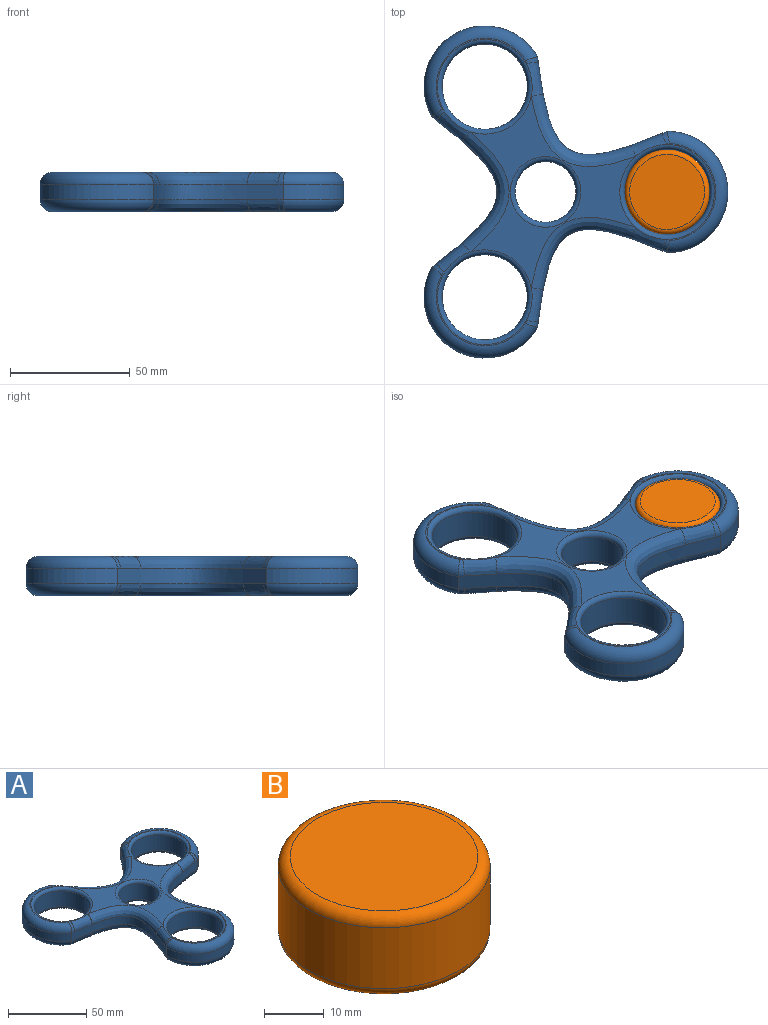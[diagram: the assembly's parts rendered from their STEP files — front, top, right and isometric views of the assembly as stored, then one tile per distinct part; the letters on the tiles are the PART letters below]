
ASSEMBLY  parts=2 mates=1
PART A: 62 faces, bbox 143x131.2x18.5 mm
  f0: plane 79.89x69.2mm, normal (0,0,1), area 1351.3mm2, adj f22,f23,f24,f25,f46,f53,f58
  f1: plane 37.59x30.43mm, normal (0,0,1), area 31.6mm2, adj f24,f57,f59,f61
  f2: plane 37.59x30.43mm, normal (0,0,1), area 31.6mm2, adj f25,f45,f47,f49
  f3: plane 79.89x69.19mm, normal (0,0,-1), area 1351.3mm2, adj f18,f19,f20,f21,f28,f35,f40
  f4: plane 37.59x30.43mm, normal (0,0,-1), area 31.6mm2, adj f21,f27,f29,f31
  f5: plane 37.59x30.43mm, normal (0,0,-1), area 31.6mm2, adj f20,f39,f41,f43
  f6: extruded ~54.2x40.99mm, area 540.5mm2, adj f7,f14,f26,f27,f28,f30,f32,f44
  f7: cylinder r=25.4mm len=50.8mm, axis (0,0,-1), area 506.7mm2, adj f6,f8,f34,f52
  f8: extruded ~54.2x40.99mm, area 540.5mm2, adj f7,f9,f36,f38,f40,f42,f43,f54
  f9: cylinder r=25.4mm len=47.4mm, axis (0,0,-1), area 506.7mm2, adj f8,f10,f41,f59
  f10: extruded ~62.59x27.08mm, area 540.5mm2, adj f9,f14,f31,f33,f35,f37,f39,f49
  f11: cylinder r=17.78mm len=35.56mm, axis (0,0,-1), area 1390.4mm2, adj f20,f24
  f12: cylinder r=17.78mm len=35.56mm, axis (0,0,-1), area 1390.4mm2, adj f21,f25
  f13: cylinder r=12.7mm len=25.4mm, axis (0,0,-1), area 993.1mm2, adj f18,f22
  f14: cylinder r=25.4mm len=47.4mm, axis (0,0,-1), area 506.7mm2, adj f6,f10,f29,f47
  f15: cylinder r=17.78mm len=35.56mm, axis (0,0,-1), area 1390.4mm2, adj f19,f23
  f16: plane 40.6x20.55mm, normal (0,0,1), area 31.6mm2, adj f23,f50,f52,f54
  f17: plane 40.6x20.55mm, normal (0,0,-1), area 31.6mm2, adj f19,f32,f34,f36
  f18: torus R=14.73mm, axis (0,0,1), area 269.5mm2, adj f3,f13
  f19: torus R=19.81mm, axis (0,0,1), area 371.4mm2, adj f3,f15,f17,f30,f38
  f20: torus R=19.81mm, axis (0,0,1), area 371.4mm2, adj f3,f5,f11,f37,f42
  f21: torus R=19.81mm, axis (0,0,1), area 371.4mm2, adj f3,f4,f12,f26,f33
  f22: torus R=14.73mm, axis (0,0,1), area 269.5mm2, adj f0,f13
  f23: torus R=19.81mm, axis (0,0,1), area 371.4mm2, adj f0,f15,f16,f48,f56
  f24: torus R=19.81mm, axis (0,0,1), area 371.4mm2, adj f0,f1,f11,f55,f60
  f25: torus R=19.81mm, axis (0,0,1), area 371.4mm2, adj f0,f2,f12,f44,f51
  f26: bspline ~17.43x8.27mm, area 97.1mm2, adj f6,f21,f27,f28
  f27: bspline ~8.75x6.12mm, area 14.4mm2, adj f4,f6,f26,f29
  f28: bspline ~46.24x33.38mm, area 449.2mm2, adj f3,f6,f26,f30
  f29: torus R=20.32mm, axis (0,0,1), area 582mm2, adj f4,f14,f27,f31
  f30: bspline ~16.58x10.79mm, area 97.1mm2, adj f6,f19,f28,f32
  f31: bspline ~12.72x11.43mm, area 14.4mm2, adj f4,f10,f29,f33
  f32: bspline ~13.13x9.3mm, area 14.4mm2, adj f6,f17,f30,f34
  f33: bspline ~15.93x14.19mm, area 97.1mm2, adj f10,f21,f31,f35
  f34: torus R=20.32mm, axis (0,0,1), area 582mm2, adj f7,f17,f32,f36
  f35: bspline ~53.88x22.07mm, area 449.2mm2, adj f3,f10,f33,f37
  f36: bspline ~9.45x7.79mm, area 14.4mm2, adj f8,f17,f34,f38
  f37: bspline ~16.09x14.46mm, area 97.1mm2, adj f10,f20,f35,f39
  f38: bspline ~17.02x10.98mm, area 97.1mm2, adj f8,f19,f36,f40
  f39: bspline ~9.55x8.99mm, area 14.4mm2, adj f5,f10,f37,f41
  f40: bspline ~47.07x32.34mm, area 449.2mm2, adj f3,f8,f38,f42
  f41: torus R=20.32mm, axis (0,0,1), area 582mm2, adj f5,f9,f39,f43
  f42: bspline ~17.88x8.2mm, area 97.1mm2, adj f8,f20,f40,f43
  f43: bspline ~12.72x6.67mm, area 14.4mm2, adj f5,f8,f41,f42
  f44: bspline ~17.97x8.53mm, area 97mm2, adj f6,f25,f45,f46
  f45: bspline ~12.72x6.67mm, area 14.4mm2, adj f2,f6,f44,f47
  f46: bspline ~47.07x32.34mm, area 449.2mm2, adj f0,f6,f44,f48
  f47: torus R=20.32mm, axis (0,0,1), area 582mm2, adj f2,f14,f45,f49
  f48: bspline ~17.02x10.98mm, area 97.1mm2, adj f6,f23,f46,f50
  f49: bspline ~9.55x8.99mm, area 14.4mm2, adj f2,f10,f47,f51
  f50: bspline ~9.45x7.79mm, area 14.4mm2, adj f6,f16,f48,f52
  f51: bspline ~15.93x14.19mm, area 97.1mm2, adj f10,f25,f49,f53
  f52: torus R=20.32mm, axis (0,0,1), area 582mm2, adj f7,f16,f50,f54
  f53: bspline ~53.88x22.07mm, area 449.2mm2, adj f0,f10,f51,f55
  f54: bspline ~13.13x9.3mm, area 14.4mm2, adj f8,f16,f52,f56
  f55: bspline ~15.7x14.07mm, area 97.1mm2, adj f10,f24,f53,f57
  f56: bspline ~16.58x10.79mm, area 97.1mm2, adj f8,f23,f54,f58
  f57: bspline ~12.72x11.43mm, area 14.4mm2, adj f1,f10,f55,f59
  f58: bspline ~46.24x33.38mm, area 449.2mm2, adj f0,f8,f56,f60
  f59: torus R=20.32mm, axis (0,0,1), area 582mm2, adj f1,f9,f57,f61
  f60: bspline ~17.47x8.11mm, area 97.1mm2, adj f8,f24,f58,f61
  f61: bspline ~8.75x6.12mm, area 14.4mm2, adj f1,f8,f59,f60
PART B: 5 faces, bbox 38.4x38.4x16.5 mm
  f0: cylinder r=17.72mm len=35.43mm, axis (0,0,-1), area 1385.4mm2, adj f3,f4
  f1: plane 31.37x31.37mm, normal (0,0,1), area 772.8mm2, adj f4
  f2: plane 31.37x31.37mm, normal (0,0,-1), area 772.8mm2, adj f3
  f3: torus R=15.68mm, axis (0,0,1), area 340.5mm2, adj f0,f2
  f4: torus R=15.68mm, axis (0,0,1), area 340.5mm2, adj f0,f1
PLACE A rot(axis=(0,0,1),90deg) t=(-55.95,-27.01,17.42)mm fixed
PLACE B t=(-5.15,-27.01,17.42)mm
MATE revolute A.f7 <-> B.f0  axis (0,0,1) through (-5.15,-27.01,33.93)mm
